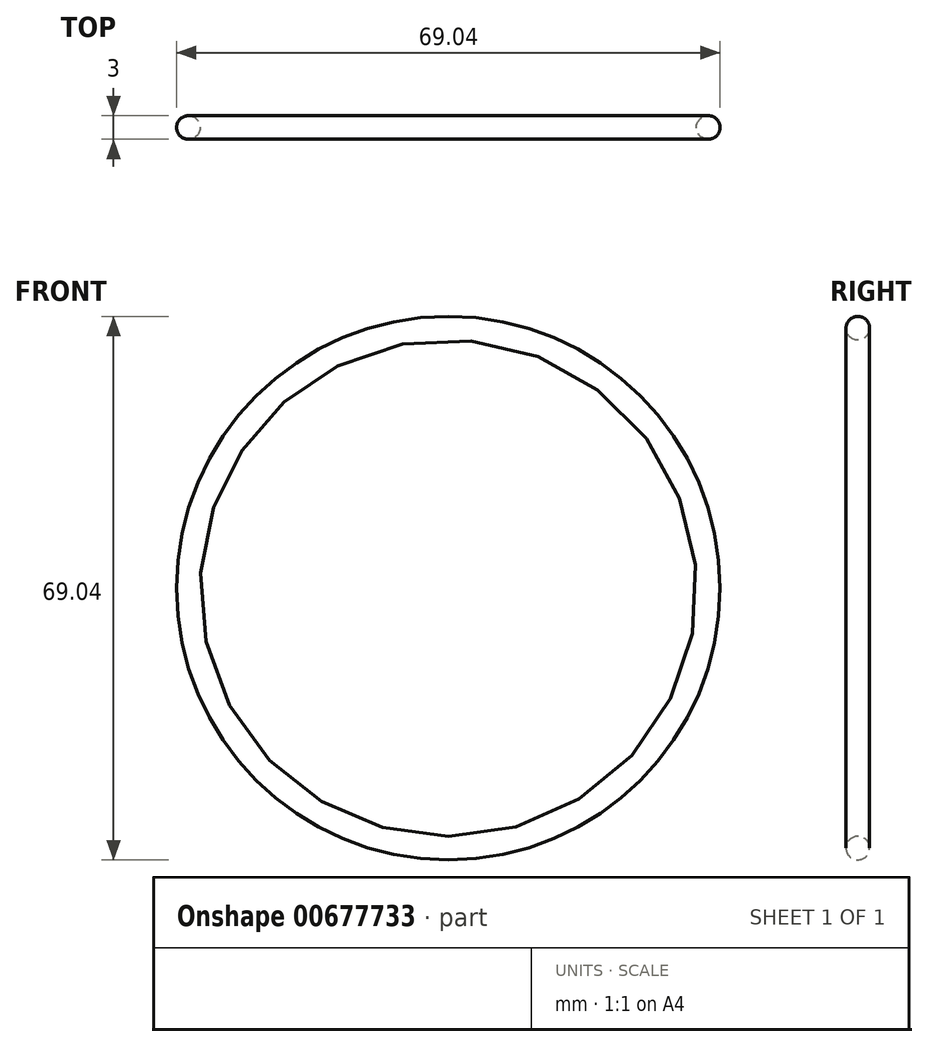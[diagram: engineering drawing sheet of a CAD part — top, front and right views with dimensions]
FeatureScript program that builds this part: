
annotation { "Feature Type Name" : "Feature", "Feature Type Description" : "" }
export const myFeature = defineFeature(function(context is Context, id is Id, definition is map)
    precondition{}
    {
        {
            var Q0;
            Q0=qCreatedBy(makeId("Front.planeOp"),FACE);
            var sketch = newSketch(context, id + "F0", { "sketchPlane" : qUnion([Q0])});
            skCircle(sketch, "E0", {"center": v(0, 0) * mm, "radius": 33.02 * mm});
            skSolve(sketch);
        }
        {
            var Q0;
            Q0=qCreatedBy(makeId("Right.planeOp"),FACE);
            var sketch = newSketch(context, id + "F1", { "sketchPlane" : qUnion([Q0])});
            skLineSegment(sketch, "E1.0", {"start": v(0, -33.02) * mm, "end": v(0, 33.02) * mm});
            skCircle(sketch, "E2", {"center": v(0, 33.02) * mm, "radius": 1.5 * mm});
            skSolve(sketch);
        }
        {
            var Q0;
            Q0=makeQuery(id+"F1.imprint","IMPRINT",FACE,{"disambiguationData":[TD([[makeQuery(id+"F1.imprint","IMPRINT",EDGE,{"derivedFrom":sQuery(id+"F1.wireOp",EDGE,"E2")}),1.0]])]});
            var Q1;
            Q1=sQuery(id+"F0.wireOp",EDGE,"E0");
            sweep(context, id + "F2", {"profiles" : qUnion([Q0]), "path" : qUnion([Q1])});
        }
    });
